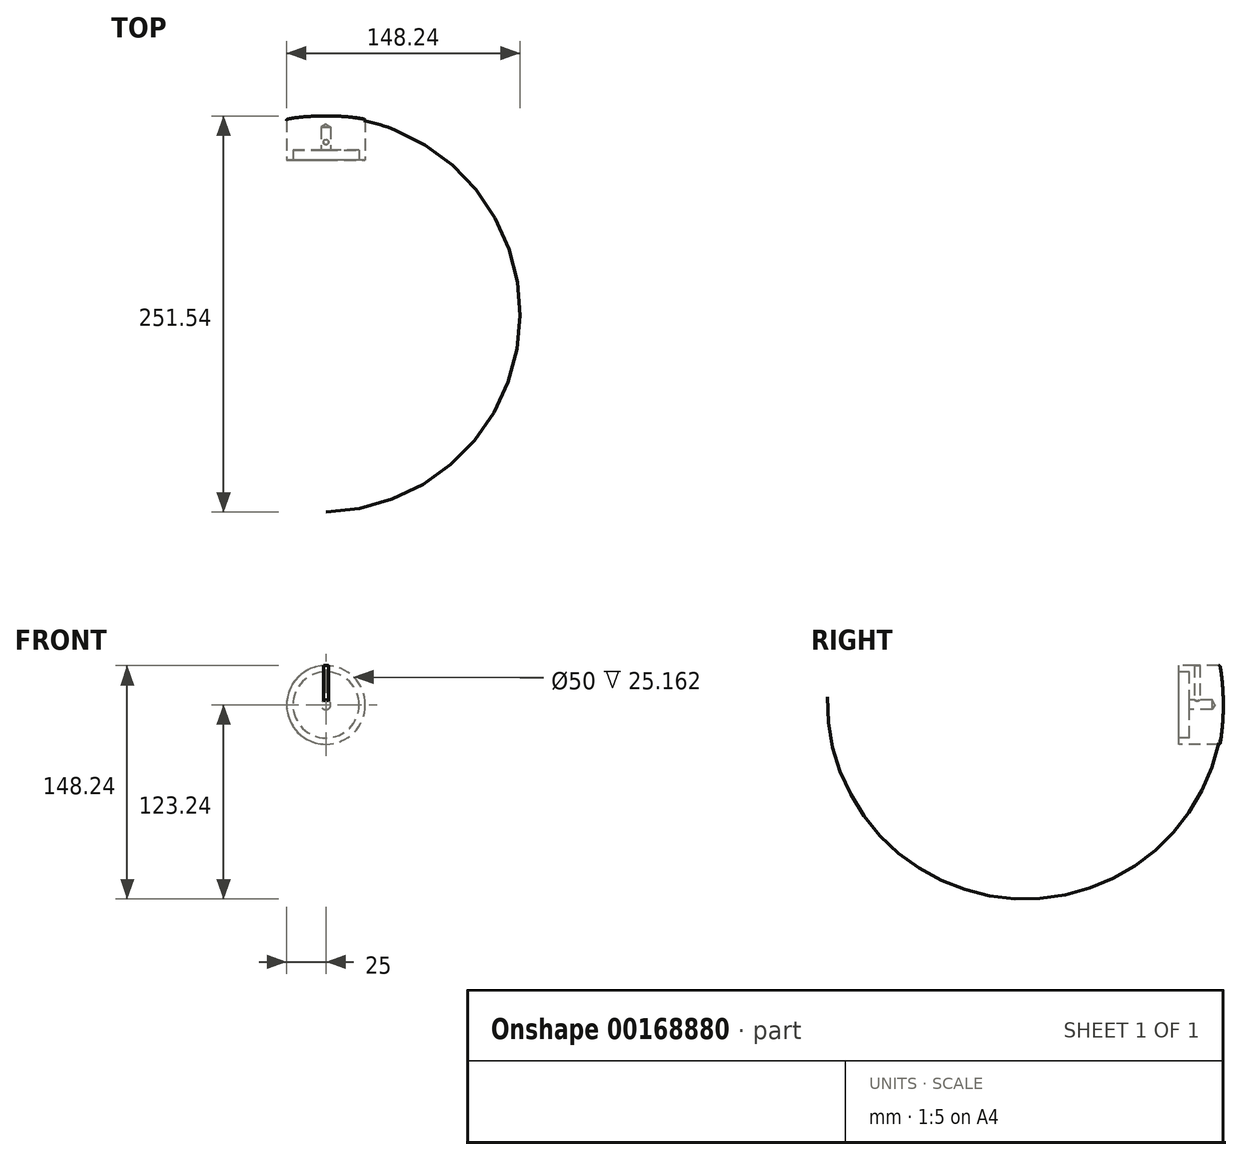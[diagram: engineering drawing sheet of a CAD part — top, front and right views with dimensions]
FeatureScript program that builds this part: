
annotation { "Feature Type Name" : "Feature", "Feature Type Description" : "" }
export const myFeature = defineFeature(function(context is Context, id is Id, definition is map)
    precondition{}
    {
        {
            var Q0;
            Q0=qCreatedBy(makeId("Front.planeOp"),FACE);
            var sketch = newSketch(context, id + "F0", { "sketchPlane" : qUnion([Q0])});
            skCircle(sketch, "E0", {"center": v(0, 0) * mm, "radius": 25 * mm});
            skSolve(sketch);
        }
        {
            var Q0;
            Q0 = qSketchRegion(id + "F0", true);
            var Q1;
            Q1 = qSketchRegion(id + "F4", true);
            extrude(context, id + "F1", {"entities" : qUnion([Q0, Q1]), "oppositeDirection" : true, "depth" : 26 * mm});
        }
        {
            var Q0;
            Q0=qCreatedBy(makeId("Front.planeOp"),FACE);
            var sketch = newSketch(context, id + "F2", { "sketchPlane" : qUnion([Q0])});
            skCircle(sketch, "E1", {"center": v(0, 0) * mm, "radius": 21 * mm});
            skSolve(sketch);
        }
        {
            var Q0;
            Q0=makeQuery(id+"F2.imprint","IMPRINT",FACE,{"disambiguationData":[TD([[makeQuery(id+"F2.imprint","IMPRINT",EDGE,{"derivedFrom":sQuery(id+"F2.wireOp",EDGE,"E1")}),1.0]])]});
            extrude(context, id + "F3", {"entities" : qUnion([Q0]), "operationType" : NewBodyOperationType.REMOVE, "oppositeDirection" : true, "depth" : 6.5 * mm});
        }
        {
            var Q0;
            Q0=makeQuery(id+"F3.boolean.opBoolean","COPY",FACE,{"derivedFrom":makeQuery(id+"F3.opExtrude","CAP_FACE",FACE,{"disambiguationData":[OSD([sQuery(id+"F2.wireOp",EDGE,"E1")])],"isStart":false})});
            var sketch = newSketch(context, id + "F4", { "sketchPlane" : qUnion([Q0])});
            skPoint(sketch, "E2", {"position": v(0, 0) * mm});
            skSolve(sketch);
        }
        {
            var Q0;
            Q0=sQuery(id+"F4.wireOp",VERTEX,"E2");
            var Q1;
            Q1=makeQuery(id+"F1.opExtrude","SWEPT_BODY",BODY,{"disambiguationData":[OSD([sQuery(id+"F0.wireOp",EDGE,"E0")])]});
            hole(context, id + "F5", {"style" : HoleStyle.SIMPLE, "endStyle" : HoleEndStyle.BLIND, "holeDiameter" : 6.05 * mm, "holeDepth" : 14.5 * mm, "startFromSketch" : true, "locations" : qUnion([Q0]), "scope" : qUnion([Q1])});
        }
        {
            var Q0;
            Q0=qCreatedBy(makeId("Top.planeOp"),FACE);
            var sketch = newSketch(context, id + "F6", { "sketchPlane" : qUnion([Q0])});
            skLineSegment(sketch, "E3", {"start": v(-20.87, 28) * mm, "end": v(0, 28) * mm, "construction": true});
            skLineSegment(sketch, "E4", {"start": v(-25, 22.36) * mm, "end": v(-25, 32.07) * mm, "construction": true});
            skArc(sketch, "E5", {"start": v(0, 28) * mm, "mid": v(-12.55, 27.62) * mm, "end": v(-25, 26) * mm});
            skLineSegment(sketch, "E6", {"start": v(0, 28) * mm, "end": v(0, 26) * mm});
            skLineSegment(sketch, "E7", {"start": v(0, 26) * mm, "end": v(-25, 26) * mm});
            skSolve(sketch);
        }
        {
            var Q0;
            Q0=makeQuery(id+"F6.imprint","IMPRINT",FACE,{"disambiguationData":[TD([[makeQuery(id+"F6.imprint","IMPRINT",EDGE,{"derivedFrom":sQuery(id+"F6.wireOp",EDGE,"E5")}),1.0]])]});
            var Q1;
            Q1=sQuery(id+"F6.wireOp",EDGE,"E6");
            revolve(context, id + "F7", {"operationType" : NewBodyOperationType.ADD, "entities" : qUnion([Q0]), "axis" : qUnion([Q1]), "revolveType" : RevolveType.FULL});
        }
        {
            var Q0;
            Q0=makeQuery(id+"F7.boolean.opBoolean","MERGE",EDGE,{"derivedFrom":[makeQuery(id+"F1.opExtrude","CAP_EDGE",EDGE,{"disambiguationData":[OSD([sQuery(id+"F0.wireOp",EDGE,"E0")])],"isStart":false}),makeQuery(id+"F7.opRevolve","SWEPT_EDGE",EDGE,{"disambiguationData":[OSD([sQuery(id+"F6.wireOp",EDGE,"E5"),sQuery(id+"F6.wireOp",EDGE,"E7")])]})]});
            fillet(context, id + "F8", {"entities" : qUnion([Q0]), "radius" : 1 * mm, "tangentPropagation" : true, "rho" : 0.5, "crossSection" : FilletCrossSection.CONIC, "allowEdgeOverflow" : false});
        }
        {
            var Q0;
            Q0=qCreatedBy(makeId("Top.planeOp"),FACE);
            var sketch = newSketch(context, id + "F9", { "sketchPlane" : qUnion([Q0])});
            skLineSegment(sketch, "E8", {"start": v(-5.48, 11.5) * mm, "end": v(39.85, 11.5) * mm, "construction": true});
            skLineSegment(sketch, "E9", {"start": v(0, 17.86) * mm, "end": v(0, -4.6) * mm, "construction": true});
            skPoint(sketch, "E10", {"position": v(0, 11.5) * mm});
            skSolve(sketch);
        }
        {
            var Q0;
            Q0=sQuery(id+"F9.wireOp",VERTEX,"E10");
            var Q1;
            Q1=makeQuery(id+"F1.opExtrude","SWEPT_BODY",BODY,{"disambiguationData":[OSD([sQuery(id+"F0.wireOp",EDGE,"E0")])]});
            hole(context, id + "F10", {"style" : HoleStyle.SIMPLE, "endStyle" : HoleEndStyle.BLIND, "oppositeDirection" : true, "standardTappedOrClearance" : lookupTablePath({ "standard" : "ISO", "fit" : "Normal", "size" : "M3", "type" : "Clearance" }), "standardBlindInLast" : lookupTablePath({ "fit" : "Standard", "standard" : "ISO", "size" : "M3", "type" : "Clearance" }), "holeDiameter" : 3.3 * mm, "holeDepth" : 25 * mm, "startFromSketch" : true, "locations" : qUnion([Q0]), "scope" : qUnion([Q1])});
        }
    });
